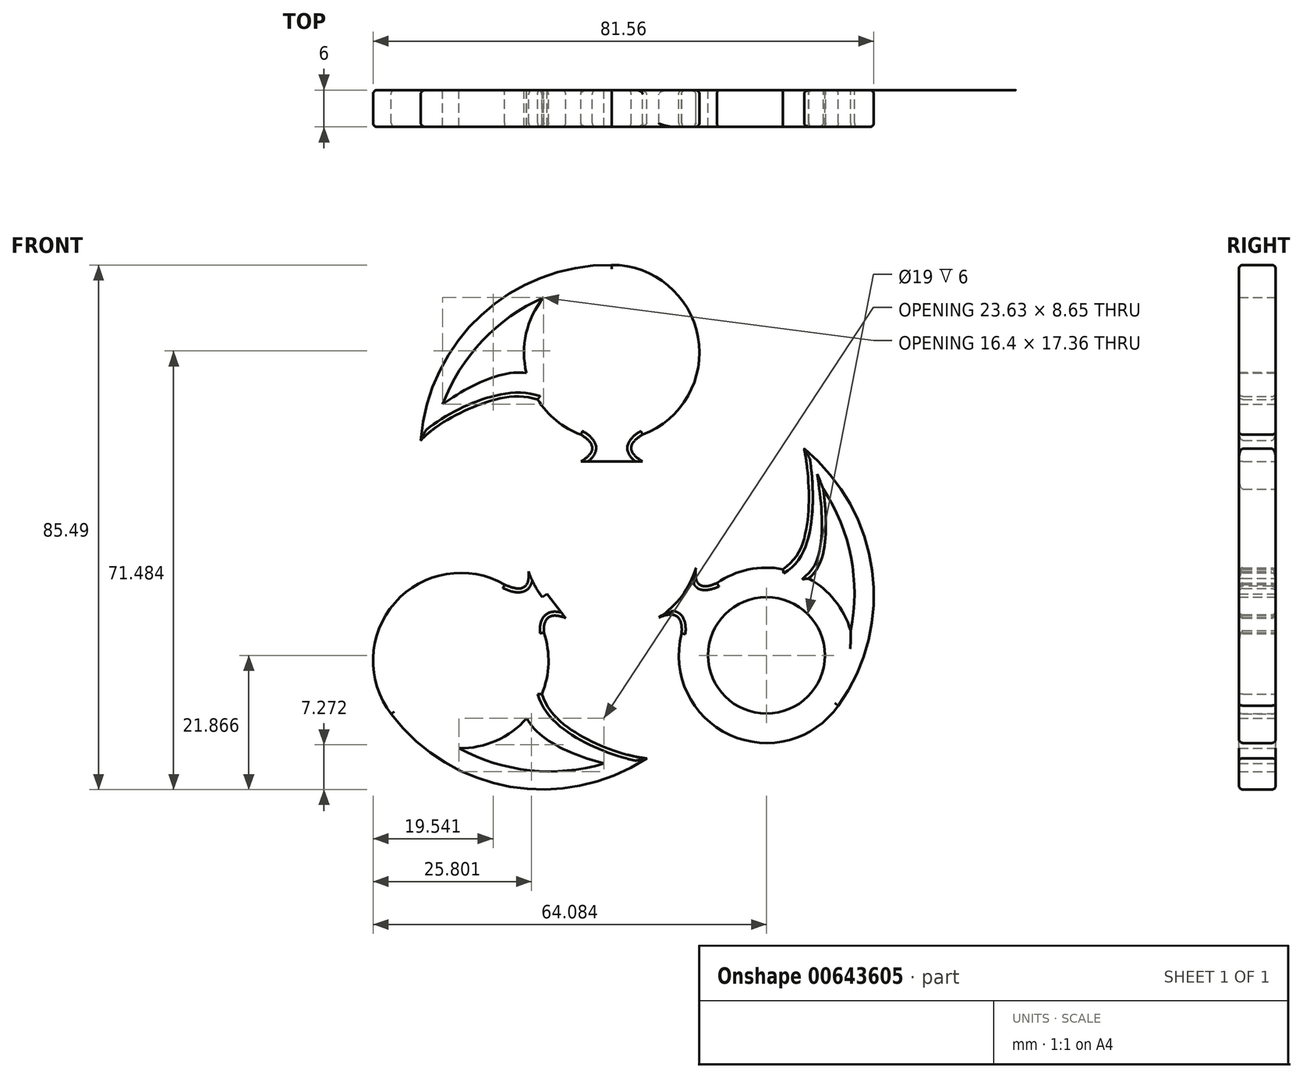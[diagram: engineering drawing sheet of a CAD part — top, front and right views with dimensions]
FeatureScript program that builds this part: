
annotation { "Feature Type Name" : "Feature", "Feature Type Description" : "" }
export const myFeature = defineFeature(function(context is Context, id is Id, definition is map)
    precondition{}
    {
        {
            var Q0;
            Q0=qCreatedBy(makeId("Front.planeOp"),FACE);
            var sketch = newSketch(context, id + "F0", { "sketchPlane" : qUnion([Q0])});
            skCircle(sketch, "E0", {"center": v(0, 0) * mm, "radius": 14.29 * mm});
            skLineSegment(sketch, "E1", {"start": v(0, 0) * mm, "end": v(0, 14.29) * mm});
            skLineSegment(sketch, "E2", {"start": v(0, 0) * mm, "end": v(-11.3, -8.76) * mm});
            skLineSegment(sketch, "E3", {"start": v(0, 0) * mm, "end": v(11.43, -8.57) * mm});
            skCircle(sketch, "E4", {"center": v(0, 31.12) * mm, "radius": 14.29 * mm});
            skLineSegment(sketch, "E5", {"start": v(0, 14.29) * mm, "end": v(0, 16.83) * mm});
            skArc(sketch, "E6", {"start": v(0, 45.4) * mm, "mid": v(-21.2, 37.27) * mm, "end": v(-31.1, 16.83) * mm});
            skFitSpline(sketch, "E7", {"points": [v(-31.1, 16.83) * mm, v(-17.35, 23.79) * mm, v(0, 16.83) * mm], "startDerivative": vector(18.3, 19.68) * mm, "endDerivative": vector(52.34, -33.11) * mm});
            skLineSegment(sketch, "E8", {"start": v(0, 15.56) * mm, "end": v(-3.18, 15.56) * mm});
            skPoint(sketch, "E8.endSnap0", {"position": v(0, 15.56) * mm});
            skLineSegment(sketch, "E9", {"start": v(0, 15.56) * mm, "end": v(3.18, 15.56) * mm});
            skLineSegment(sketch, "E10", {"start": v(0, 17.74) * mm, "end": v(5.03, 17.74) * mm});
            skLineSegment(sketch, "E11", {"start": v(0, 17.74) * mm, "end": v(-5.03, 17.74) * mm});
            skLineSegment(sketch, "E12", {"start": v(0, 14.29) * mm, "end": v(0, 13.37) * mm});
            skLineSegment(sketch, "E13", {"start": v(0, 13.37) * mm, "end": v(-5.03, 13.37) * mm});
            skLineSegment(sketch, "E14", {"start": v(0, 13.37) * mm, "end": v(5.03, 13.37) * mm});
            skFitSpline(sketch, "E15", {"points": [v(-5.03, 17.74) * mm, v(-3.18, 15.56) * mm, v(-5.03, 13.37) * mm], "startDerivative": vector(7.47, -4.37) * mm, "endDerivative": vector(-7.47, -4.37) * mm});
            skFitSpline(sketch, "E16", {"points": [v(5.03, 13.37) * mm, v(3.18, 15.56) * mm, v(5.03, 17.74) * mm], "startDerivative": vector(-7.47, 4.37) * mm, "endDerivative": vector(7.47, 4.37) * mm});
            skArc(sketch, "E17", {"start": v(4.36, 42.56) * mm, "mid": v(-16.61, 36.94) * mm, "end": v(-28.69, 18.9) * mm});
            skFitSpline(sketch, "E18", {"points": [v(-30.7, 19.98) * mm, v(-16.8, 27.72) * mm, v(0.44, 19.97) * mm], "startDerivative": vector(18.3, 19.68) * mm, "endDerivative": vector(52.34, -33.11) * mm});
            skLineSegment(sketch, "E19", {"start": v(-3.18, 15.56) * mm, "end": v(0, 14.29) * mm});
            skLineSegment(sketch, "E20", {"start": v(0, 14.29) * mm, "end": v(3.18, 15.56) * mm});
            skCircle(sketch, "E21", {"center": v(25.21, -18.22) * mm, "radius": 14.29 * mm});
            skLineSegment(sketch, "E22", {"start": v(11.43, -8.57) * mm, "end": v(13.51, -10.03) * mm});
            skArc(sketch, "E23", {"start": v(36.92, -26.42) * mm, "mid": v(42.42, -4.39) * mm, "end": v(31.34, 15.44) * mm});
            skFitSpline(sketch, "E24", {"points": [v(31.34, 15.44) * mm, v(30.71, -0.93) * mm, v(13.51, -10.03) * mm], "startDerivative": vector(5.62, -26.28) * mm, "endDerivative": vector(-57.15, -23.88) * mm});
            skLineSegment(sketch, "E25", {"start": v(12.47, -9.3) * mm, "end": v(14.3, -6.7) * mm});
            skPoint(sketch, "E25.endSnap0", {"position": v(12.47, -9.3) * mm});
            skLineSegment(sketch, "E26", {"start": v(12.47, -9.3) * mm, "end": v(10.65, -11.9) * mm});
            skLineSegment(sketch, "E27", {"start": v(14.26, -10.55) * mm, "end": v(11.38, -14.67) * mm});
            skLineSegment(sketch, "E28", {"start": v(14.26, -10.55) * mm, "end": v(17.14, -6.43) * mm});
            skArc(sketch, "E29", {"start": v(32.04, -28.23) * mm, "mid": v(39.54, -7.93) * mm, "end": v(31.84, 12.3) * mm});
            skFitSpline(sketch, "E30", {"points": [v(33.7, 13.3) * mm, v(33.83, -3.4) * mm, v(15.84, -12.2) * mm], "startDerivative": vector(5.62, -26.28) * mm, "endDerivative": vector(-57.15, -23.88) * mm});
            skLineSegment(sketch, "E31", {"start": v(14.3, -6.7) * mm, "end": v(11.8, -8.05) * mm});
            skLineSegment(sketch, "E32", {"start": v(11.43, -8.57) * mm, "end": v(10.65, -11.9) * mm});
            skLineSegment(sketch, "E33.0", {"start": v(14.3, -6.7) * mm, "end": v(12.47, -9.3) * mm, "construction": true});
            skCircle(sketch, "E34", {"center": v(-24.58, -19.07) * mm, "radius": 14.29 * mm});
            skLineSegment(sketch, "E35", {"start": v(-11.3, -8.76) * mm, "end": v(-13.26, -10.36) * mm});
            skArc(sketch, "E36", {"start": v(-35.91, -27.78) * mm, "mid": v(-16.54, -39.63) * mm, "end": v(5.7, -35.02) * mm});
            skFitSpline(sketch, "E37", {"points": [v(5.7, -35.02) * mm, v(-8.63, -28.76) * mm, v(-13.26, -10.36) * mm], "startDerivative": vector(-26.76, 2.52) * mm, "endDerivative": vector(-5.64, 61.68) * mm});
            skLineSegment(sketch, "E38", {"start": v(-12.27, -9.56) * mm, "end": v(-10.26, -12.02) * mm});
            skPoint(sketch, "E38.endSnap0", {"position": v(-12.27, -9.56) * mm});
            skLineSegment(sketch, "E39", {"start": v(-12.27, -9.56) * mm, "end": v(-14.28, -7.1) * mm});
            skLineSegment(sketch, "E40", {"start": v(-13.97, -10.94) * mm, "end": v(-17.43, -6.7) * mm});
            skLineSegment(sketch, "E41", {"start": v(-13.97, -10.94) * mm, "end": v(-11.04, -14.51) * mm});
            skArc(sketch, "E42", {"start": v(-36.27, -22.58) * mm, "mid": v(-19.07, -35.8) * mm, "end": v(2.57, -34.43) * mm});
            skFitSpline(sketch, "E43", {"points": [v(2.95, -36.62) * mm, v(-12.05, -30.77) * mm, v(-16.16, -11.65) * mm], "startDerivative": vector(-26.76, 2.52) * mm, "endDerivative": vector(-5.64, 61.68) * mm});
            skLineSegment(sketch, "E44", {"start": v(-10.26, -12.02) * mm, "end": v(-10.8, -9.23) * mm});
            skLineSegment(sketch, "E45", {"start": v(-11.3, -8.76) * mm, "end": v(-14.28, -7.1) * mm});
            skLineSegment(sketch, "E46.0", {"start": v(-10.26, -12.02) * mm, "end": v(-12.27, -9.56) * mm, "construction": true});
            skLineSegment(sketch, "E47", {"start": v(-11.3, -8.76) * mm, "end": v(-10.57, -8.2) * mm});
            skLineSegment(sketch, "E48", {"start": v(11.43, -8.57) * mm, "end": v(10.7, -8.02) * mm});
            skLineSegment(sketch, "E49", {"start": v(10.7, -8.02) * mm, "end": v(13.72, -4) * mm});
            skLineSegment(sketch, "E50", {"start": v(10.7, -8.02) * mm, "end": v(7.68, -12.05) * mm});
            skLineSegment(sketch, "E51", {"start": v(-10.57, -8.2) * mm, "end": v(-13.54, -4.56) * mm});
            skLineSegment(sketch, "E52", {"start": v(-10.57, -8.2) * mm, "end": v(-7.49, -12.17) * mm});
            skFitSpline(sketch, "E53", {"points": [v(-13.54, -4.56) * mm, v(-14.28, -7.1) * mm, v(-17.43, -6.7) * mm], "startDerivative": vector(0.73, -8.28) * mm, "endDerivative": vector(-8.38, 3.81) * mm});
            skFitSpline(sketch, "E54", {"points": [v(-11.04, -14.51) * mm, v(-10.26, -12.02) * mm, v(-7.49, -12.17) * mm], "startDerivative": vector(-0.57, 7.9) * mm, "endDerivative": vector(7.64, -3.14) * mm});
            skFitSpline(sketch, "E55", {"points": [v(7.68, -12.05) * mm, v(10.65, -11.9) * mm, v(11.38, -14.67) * mm], "startDerivative": vector(8.1, 3.32) * mm, "endDerivative": vector(-0.74, -8.6) * mm});
            skFitSpline(sketch, "E56", {"points": [v(13.72, -4) * mm, v(14.3, -6.7) * mm, v(17.14, -6.43) * mm], "startDerivative": vector(-1.06, -8.48) * mm, "endDerivative": vector(7.9, 3.59) * mm});
            skSolve(sketch);
        }
        {
            var Q0;
            {var subQ0=sQuery(id+"F0.wireOp",EDGE,"E6");var subQ1=sQuery(id+"F0.wireOp",EDGE,"E4");var subQ2=makeQuery(id+"F0.imprint","INTERSECT",VERTEX,{"derivedFrom":[subQ1,subQ0]});Q0=makeQuery(id+"F0.imprint","IMPRINT",FACE,{"disambiguationData":[TD([[makeQuery(id+"F0.imprint","IMPRINT",EDGE,{"disambiguationData":[TD([[subQ2,-1.0]])],"derivedFrom":subQ1}),-1.0]])]});}
            var Q1;
            {var subQ0=sQuery(id+"F0.wireOp",EDGE,"E18");var subQ1=sQuery(id+"F0.wireOp",EDGE,"E4");var subQ2=makeQuery(id+"F0.imprint","INTERSECT",VERTEX,{"derivedFrom":[subQ1,subQ0]});Q1=makeQuery(id+"F0.imprint","IMPRINT",FACE,{"disambiguationData":[TD([[makeQuery(id+"F0.imprint","IMPRINT",EDGE,{"disambiguationData":[TD([[subQ2,-1.0]])],"derivedFrom":subQ1}),-1.0]])]});}
            var Q2;
            {var subQ0=sQuery(id+"F0.wireOp",EDGE,"E7");var subQ1=sQuery(id+"F0.wireOp",EDGE,"E6");var subQ2=makeQuery(id+"F0.imprint","INTERSECT",VERTEX,{"derivedFrom":[subQ1,subQ0]});Q2=makeQuery(id+"F0.imprint","IMPRINT",FACE,{"disambiguationData":[TD([[makeQuery(id+"F0.imprint","IMPRINT",EDGE,{"disambiguationData":[TD([[subQ2,1.0]])],"derivedFrom":subQ1}),1.0]])]});}
            var Q3;
            {var subQ7=sQuery(id+"F0.wireOp",EDGE,"E10");Q3=makeQuery(id+"F0.imprint","IMPRINT",FACE,{"disambiguationData":[TD([[makeQuery(id+"F0.imprint","IMPRINT",EDGE,{"derivedFrom":subQ7}),1.0]])]});}
            var Q4;
            Q4=makeQuery(id+"F0.imprint","IMPRINT",FACE,{"disambiguationData":[TD([[makeQuery(id+"F0.imprint","IMPRINT",EDGE,{"derivedFrom":sQuery(id+"F0.wireOp",EDGE,"E1")}),1.0]])]});
            var Q5;
            Q5=makeQuery(id+"F0.imprint","IMPRINT",FACE,{"disambiguationData":[TD([[makeQuery(id+"F0.imprint","IMPRINT",EDGE,{"derivedFrom":sQuery(id+"F0.wireOp",EDGE,"E2")}),1.0]])]});
            var Q6;
            Q6=makeQuery(id+"F0.imprint","IMPRINT",FACE,{"disambiguationData":[TD([[makeQuery(id+"F0.imprint","IMPRINT",EDGE,{"derivedFrom":sQuery(id+"F0.wireOp",EDGE,"E1")}),-1.0]])]});
            var Q7;
            {var subQ7=sQuery(id+"F0.wireOp",EDGE,"E40");Q7=makeQuery(id+"F0.imprint","IMPRINT",FACE,{"disambiguationData":[TD([[makeQuery(id+"F0.imprint","IMPRINT",EDGE,{"derivedFrom":subQ7}),1.0]])]});}
            var Q8;
            {var subQ0=sQuery(id+"F0.wireOp",EDGE,"E36");var subQ1=sQuery(id+"F0.wireOp",EDGE,"E34");var subQ2=makeQuery(id+"F0.imprint","INTERSECT",VERTEX,{"derivedFrom":[subQ1,subQ0]});Q8=makeQuery(id+"F0.imprint","IMPRINT",FACE,{"disambiguationData":[TD([[makeQuery(id+"F0.imprint","IMPRINT",EDGE,{"disambiguationData":[TD([[subQ2,-1.0]])],"derivedFrom":subQ1}),-1.0]])]});}
            var Q9;
            {var subQ0=sQuery(id+"F0.wireOp",EDGE,"E43");var subQ1=sQuery(id+"F0.wireOp",EDGE,"E34");var subQ2=makeQuery(id+"F0.imprint","INTERSECT",VERTEX,{"derivedFrom":[subQ1,subQ0]});Q9=makeQuery(id+"F0.imprint","IMPRINT",FACE,{"disambiguationData":[TD([[makeQuery(id+"F0.imprint","IMPRINT",EDGE,{"disambiguationData":[TD([[subQ2,-1.0]])],"derivedFrom":subQ1}),-1.0]])]});}
            var Q10;
            {var subQ0=sQuery(id+"F0.wireOp",EDGE,"E37");var subQ1=sQuery(id+"F0.wireOp",EDGE,"E36");var subQ2=makeQuery(id+"F0.imprint","INTERSECT",VERTEX,{"derivedFrom":[subQ1,subQ0]});Q10=makeQuery(id+"F0.imprint","IMPRINT",FACE,{"disambiguationData":[TD([[makeQuery(id+"F0.imprint","IMPRINT",EDGE,{"disambiguationData":[TD([[subQ2,1.0]])],"derivedFrom":subQ1}),1.0]])]});}
            var Q11;
            {var subQ1=sQuery(id+"F0.wireOp",EDGE,"E34");var subQ3=sQuery(id+"F0.wireOp",EDGE,"E37");var subQ4=makeQuery(id+"F0.imprint","INTERSECT",VERTEX,{"derivedFrom":[subQ1,subQ3]});Q11=makeQuery(id+"F0.imprint","IMPRINT",FACE,{"disambiguationData":[TD([[makeQuery(id+"F0.imprint","IMPRINT",EDGE,{"disambiguationData":[TD([[subQ4,-1.0]])],"derivedFrom":subQ3}),-1.0]])]});}
            var Q12;
            {var subQ5=sQuery(id+"F0.wireOp",EDGE,"E27");Q12=makeQuery(id+"F0.imprint","IMPRINT",FACE,{"disambiguationData":[TD([[makeQuery(id+"F0.imprint","IMPRINT",EDGE,{"derivedFrom":subQ5}),1.0]])]});}
            var Q13;
            {var subQ0=sQuery(id+"F0.wireOp",EDGE,"E23");var subQ1=sQuery(id+"F0.wireOp",EDGE,"E21");var subQ2=makeQuery(id+"F0.imprint","INTERSECT",VERTEX,{"derivedFrom":[subQ1,subQ0]});Q13=makeQuery(id+"F0.imprint","IMPRINT",FACE,{"disambiguationData":[TD([[makeQuery(id+"F0.imprint","IMPRINT",EDGE,{"disambiguationData":[TD([[subQ2,-1.0]])],"derivedFrom":subQ1}),-1.0]])]});}
            var Q14;
            {var subQ0=sQuery(id+"F0.wireOp",EDGE,"E30");var subQ1=sQuery(id+"F0.wireOp",EDGE,"E21");var subQ2=makeQuery(id+"F0.imprint","INTERSECT",VERTEX,{"derivedFrom":[subQ1,subQ0]});Q14=makeQuery(id+"F0.imprint","IMPRINT",FACE,{"disambiguationData":[TD([[makeQuery(id+"F0.imprint","IMPRINT",EDGE,{"disambiguationData":[TD([[subQ2,-1.0]])],"derivedFrom":subQ1}),-1.0]])]});}
            var Q15;
            {var subQ0=sQuery(id+"F0.wireOp",EDGE,"E24");var subQ1=sQuery(id+"F0.wireOp",EDGE,"E23");var subQ2=makeQuery(id+"F0.imprint","INTERSECT",VERTEX,{"derivedFrom":[subQ1,subQ0]});Q15=makeQuery(id+"F0.imprint","IMPRINT",FACE,{"disambiguationData":[TD([[makeQuery(id+"F0.imprint","IMPRINT",EDGE,{"disambiguationData":[TD([[subQ2,1.0]])],"derivedFrom":subQ1}),1.0]])]});}
            var Q16;
            {var subQ0=sQuery(id+"F0.wireOp",EDGE,"E28");var subQ1=sQuery(id+"F0.wireOp",EDGE,"E21");var subQ2=makeQuery(id+"F0.imprint","INTERSECT",VERTEX,{"derivedFrom":[subQ1,subQ0]});Q16=makeQuery(id+"F0.imprint","IMPRINT",FACE,{"disambiguationData":[TD([[makeQuery(id+"F0.imprint","IMPRINT",EDGE,{"disambiguationData":[TD([[subQ2,1.0]])],"derivedFrom":subQ1}),1.0]])]});}
            var Q17;
            {var subQ3=sQuery(id+"F0.wireOp",EDGE,"E40");Q17=makeQuery(id+"F0.imprint","IMPRINT",FACE,{"disambiguationData":[TD([[makeQuery(id+"F0.imprint","IMPRINT",EDGE,{"derivedFrom":subQ3}),-1.0]])]});}
            var Q18;
            {var subQ0=sQuery(id+"F0.wireOp",EDGE,"E37");var subQ3=sQuery(id+"F0.wireOp",EDGE,"E41");var subQ5=makeQuery(id+"F0.imprint","INTERSECT",VERTEX,{"derivedFrom":[subQ0,subQ3]});Q18=makeQuery(id+"F0.imprint","IMPRINT",FACE,{"disambiguationData":[TD([[makeQuery(id+"F0.imprint","IMPRINT",EDGE,{"disambiguationData":[TD([[subQ5,-1.0]])],"derivedFrom":subQ0}),-1.0]])]});}
            var Q19;
            {var subQ0=sQuery(id+"F0.wireOp",EDGE,"E47");Q19=makeQuery(id+"F0.imprint","IMPRINT",FACE,{"disambiguationData":[TD([[makeQuery(id+"F0.imprint","IMPRINT",EDGE,{"derivedFrom":subQ0}),-1.0]])]});}
            var Q20;
            {var subQ0=sQuery(id+"F0.wireOp",EDGE,"E47");Q20=makeQuery(id+"F0.imprint","IMPRINT",FACE,{"disambiguationData":[TD([[makeQuery(id+"F0.imprint","IMPRINT",EDGE,{"derivedFrom":subQ0}),1.0]])]});}
            var Q21;
            {var subQ0=sQuery(id+"F0.wireOp",EDGE,"E45");Q21=makeQuery(id+"F0.imprint","IMPRINT",FACE,{"disambiguationData":[TD([[makeQuery(id+"F0.imprint","IMPRINT",EDGE,{"derivedFrom":subQ0}),-1.0]])]});}
            var Q22;
            {var subQ1=sQuery(id+"F0.wireOp",EDGE,"E0");var subQ3=sQuery(id+"F0.wireOp",EDGE,"E44");var subQ4=makeQuery(id+"F0.imprint","INTERSECT",VERTEX,{"derivedFrom":[subQ1,subQ3]});Q22=makeQuery(id+"F0.imprint","IMPRINT",FACE,{"disambiguationData":[TD([[makeQuery(id+"F0.imprint","IMPRINT",EDGE,{"disambiguationData":[TD([[subQ4,-1.0]])],"derivedFrom":subQ1}),-1.0]])]});}
            var Q23;
            {var subQ5=sQuery(id+"F0.wireOp",EDGE,"E38");Q23=makeQuery(id+"F0.imprint","IMPRINT",FACE,{"disambiguationData":[TD([[makeQuery(id+"F0.imprint","IMPRINT",EDGE,{"derivedFrom":subQ5}),-1.0]])]});}
            var Q24;
            {var subQ5=sQuery(id+"F0.wireOp",EDGE,"E39");Q24=makeQuery(id+"F0.imprint","IMPRINT",FACE,{"disambiguationData":[TD([[makeQuery(id+"F0.imprint","IMPRINT",EDGE,{"derivedFrom":subQ5}),1.0]])]});}
            var Q25;
            {var subQ2=sQuery(id+"F0.wireOp",EDGE,"E39");Q25=makeQuery(id+"F0.imprint","IMPRINT",FACE,{"disambiguationData":[TD([[makeQuery(id+"F0.imprint","IMPRINT",EDGE,{"derivedFrom":subQ2}),-1.0]])]});}
            var Q26;
            {var subQ5=sQuery(id+"F0.wireOp",EDGE,"E38");Q26=makeQuery(id+"F0.imprint","IMPRINT",FACE,{"disambiguationData":[TD([[makeQuery(id+"F0.imprint","IMPRINT",EDGE,{"derivedFrom":subQ5}),1.0]])]});}
            var Q27;
            {var subQ3=sQuery(id+"F0.wireOp",EDGE,"E27");Q27=makeQuery(id+"F0.imprint","IMPRINT",FACE,{"disambiguationData":[TD([[makeQuery(id+"F0.imprint","IMPRINT",EDGE,{"derivedFrom":subQ3}),-1.0]])]});}
            var Q28;
            {var subQ0=sQuery(id+"F0.wireOp",EDGE,"E24");var subQ3=sQuery(id+"F0.wireOp",EDGE,"E28");var subQ5=makeQuery(id+"F0.imprint","INTERSECT",VERTEX,{"derivedFrom":[subQ0,subQ3]});Q28=makeQuery(id+"F0.imprint","IMPRINT",FACE,{"disambiguationData":[TD([[makeQuery(id+"F0.imprint","IMPRINT",EDGE,{"disambiguationData":[TD([[subQ5,-1.0]])],"derivedFrom":subQ0}),-1.0]])]});}
            var Q29;
            {var subQ5=sQuery(id+"F0.wireOp",EDGE,"E25");Q29=makeQuery(id+"F0.imprint","IMPRINT",FACE,{"disambiguationData":[TD([[makeQuery(id+"F0.imprint","IMPRINT",EDGE,{"derivedFrom":subQ5}),-1.0]])]});}
            var Q30;
            {var subQ2=sQuery(id+"F0.wireOp",EDGE,"E25");Q30=makeQuery(id+"F0.imprint","IMPRINT",FACE,{"disambiguationData":[TD([[makeQuery(id+"F0.imprint","IMPRINT",EDGE,{"derivedFrom":subQ2}),1.0]])]});}
            var Q31;
            {var subQ0=sQuery(id+"F0.wireOp",EDGE,"E31");Q31=makeQuery(id+"F0.imprint","IMPRINT",FACE,{"disambiguationData":[TD([[makeQuery(id+"F0.imprint","IMPRINT",EDGE,{"derivedFrom":subQ0}),-1.0]])]});}
            var Q32;
            {var subQ0=sQuery(id+"F0.wireOp",EDGE,"E48");Q32=makeQuery(id+"F0.imprint","IMPRINT",FACE,{"disambiguationData":[TD([[makeQuery(id+"F0.imprint","IMPRINT",EDGE,{"derivedFrom":subQ0}),-1.0]])]});}
            var Q33;
            {var subQ0=sQuery(id+"F0.wireOp",EDGE,"E48");Q33=makeQuery(id+"F0.imprint","IMPRINT",FACE,{"disambiguationData":[TD([[makeQuery(id+"F0.imprint","IMPRINT",EDGE,{"derivedFrom":subQ0}),1.0]])]});}
            var Q34;
            {var subQ0=sQuery(id+"F0.wireOp",EDGE,"E32");Q34=makeQuery(id+"F0.imprint","IMPRINT",FACE,{"disambiguationData":[TD([[makeQuery(id+"F0.imprint","IMPRINT",EDGE,{"derivedFrom":subQ0}),-1.0]])]});}
            var Q35;
            {var subQ2=sQuery(id+"F0.wireOp",EDGE,"E26");Q35=makeQuery(id+"F0.imprint","IMPRINT",FACE,{"disambiguationData":[TD([[makeQuery(id+"F0.imprint","IMPRINT",EDGE,{"derivedFrom":subQ2}),-1.0]])]});}
            var Q36;
            {var subQ5=sQuery(id+"F0.wireOp",EDGE,"E26");Q36=makeQuery(id+"F0.imprint","IMPRINT",FACE,{"disambiguationData":[TD([[makeQuery(id+"F0.imprint","IMPRINT",EDGE,{"derivedFrom":subQ5}),1.0]])]});}
            var Q37;
            {var subQ1=sQuery(id+"F0.wireOp",EDGE,"E4");var subQ3=sQuery(id+"F0.wireOp",EDGE,"E7");var subQ4=makeQuery(id+"F0.imprint","INTERSECT",VERTEX,{"derivedFrom":[subQ1,subQ3]});Q37=makeQuery(id+"F0.imprint","IMPRINT",FACE,{"disambiguationData":[TD([[makeQuery(id+"F0.imprint","IMPRINT",EDGE,{"disambiguationData":[TD([[subQ4,-1.0]])],"derivedFrom":subQ3}),-1.0]])]});}
            var Q38;
            {var subQ0=sQuery(id+"F0.wireOp",EDGE,"E7");var subQ3=sQuery(id+"F0.wireOp",EDGE,"E11");var subQ5=makeQuery(id+"F0.imprint","INTERSECT",VERTEX,{"derivedFrom":[subQ0,subQ3]});Q38=makeQuery(id+"F0.imprint","IMPRINT",FACE,{"disambiguationData":[TD([[makeQuery(id+"F0.imprint","IMPRINT",EDGE,{"disambiguationData":[TD([[subQ5,-1.0]])],"derivedFrom":subQ0}),-1.0]])]});}
            var Q39;
            {var subQ5=sQuery(id+"F0.wireOp",EDGE,"E8");Q39=makeQuery(id+"F0.imprint","IMPRINT",FACE,{"disambiguationData":[TD([[makeQuery(id+"F0.imprint","IMPRINT",EDGE,{"derivedFrom":subQ5}),-1.0]])]});}
            var Q40;
            {var subQ0=sQuery(id+"F0.wireOp",EDGE,"E20");Q40=makeQuery(id+"F0.imprint","IMPRINT",FACE,{"disambiguationData":[TD([[makeQuery(id+"F0.imprint","IMPRINT",EDGE,{"derivedFrom":subQ0}),-1.0]])]});}
            var Q41;
            {var subQ0=sQuery(id+"F0.wireOp",EDGE,"E12");Q41=makeQuery(id+"F0.imprint","IMPRINT",FACE,{"disambiguationData":[TD([[makeQuery(id+"F0.imprint","IMPRINT",EDGE,{"derivedFrom":subQ0}),1.0]])]});}
            var Q42;
            {var subQ0=sQuery(id+"F0.wireOp",EDGE,"E12");Q42=makeQuery(id+"F0.imprint","IMPRINT",FACE,{"disambiguationData":[TD([[makeQuery(id+"F0.imprint","IMPRINT",EDGE,{"derivedFrom":subQ0}),-1.0]])]});}
            var Q43;
            {var subQ0=sQuery(id+"F0.wireOp",EDGE,"E19");Q43=makeQuery(id+"F0.imprint","IMPRINT",FACE,{"disambiguationData":[TD([[makeQuery(id+"F0.imprint","IMPRINT",EDGE,{"derivedFrom":subQ0}),-1.0]])]});}
            var Q44;
            {var subQ2=sQuery(id+"F0.wireOp",EDGE,"E8");Q44=makeQuery(id+"F0.imprint","IMPRINT",FACE,{"disambiguationData":[TD([[makeQuery(id+"F0.imprint","IMPRINT",EDGE,{"derivedFrom":subQ2}),1.0]])]});}
            var Q45;
            {var subQ2=sQuery(id+"F0.wireOp",EDGE,"E9");Q45=makeQuery(id+"F0.imprint","IMPRINT",FACE,{"disambiguationData":[TD([[makeQuery(id+"F0.imprint","IMPRINT",EDGE,{"derivedFrom":subQ2}),-1.0]])]});}
            var Q46;
            {var subQ5=sQuery(id+"F0.wireOp",EDGE,"E9");Q46=makeQuery(id+"F0.imprint","IMPRINT",FACE,{"disambiguationData":[TD([[makeQuery(id+"F0.imprint","IMPRINT",EDGE,{"derivedFrom":subQ5}),1.0]])]});}
            var Q47;
            {var subQ3=sQuery(id+"F0.wireOp",EDGE,"E10");Q47=makeQuery(id+"F0.imprint","IMPRINT",FACE,{"disambiguationData":[TD([[makeQuery(id+"F0.imprint","IMPRINT",EDGE,{"derivedFrom":subQ3}),-1.0]])]});}
            extrude(context, id + "F1", {"entities" : qUnion([Q0, Q1, Q2, Q3, Q4, Q5, Q6, Q7, Q8, Q9, Q10, Q11, Q12, Q13, Q14, Q15, Q16, Q17, Q18, Q19, Q20, Q21, Q22, Q23, Q24, Q25, Q26, Q27, Q28, Q29, Q30, Q31, Q32, Q33, Q34, Q35, Q36, Q37, Q38, Q39, Q40, Q41, Q42, Q43, Q44, Q45, Q46, Q47]), "depth" : 6 * mm, "offsetDistance" : 25.4 * mm});
        }
        {
            var Q0;
            {var subQ0=sQuery(id+"F0.wireOp",EDGE,"E4");Q0=makeQuery(id+"F1.opExtrude","CAP_EDGE",EDGE,{"disambiguationData":[OSD([subQ0]),TDD([makeQuery(id+"F0.imprint","IMPRINT",EDGE,{"disambiguationData":[TD([[makeQuery(id+"F0.imprint","INTERSECT",VERTEX,{"derivedFrom":[subQ0,sQuery(id+"F0.wireOp",EDGE,"E7")]}),-1.0]])],"derivedFrom":subQ0})])],"isStart":false});}
            var Q1;
            Q1=makeQuery(id+"F1.opExtrude","CAP_EDGE",EDGE,{"disambiguationData":[OSD([sQuery(id+"F0.wireOp",EDGE,"E15")])],"isStart":false});
            var Q2;
            {var subQ0=sQuery(id+"F0.wireOp",EDGE,"E0");Q2=makeQuery(id+"F1.opExtrude","CAP_EDGE",EDGE,{"disambiguationData":[OSD([subQ0]),TDD([makeQuery(id+"F0.imprint","IMPRINT",EDGE,{"disambiguationData":[TD([[makeQuery(id+"F0.imprint","INTERSECT",VERTEX,{"derivedFrom":[subQ0,sQuery(id+"F0.wireOp",EDGE,"E13"),sQuery(id+"F0.wireOp",EDGE,"E15")]}),-1.0]])],"derivedFrom":subQ0})])],"isStart":false});}
            var Q3;
            Q3=makeQuery(id+"F1.opExtrude","CAP_EDGE",EDGE,{"disambiguationData":[OSD([sQuery(id+"F0.wireOp",EDGE,"E53")])],"isStart":false});
            var Q4;
            {var subQ0=sQuery(id+"F0.wireOp",EDGE,"E34");Q4=makeQuery(id+"F1.opExtrude","CAP_EDGE",EDGE,{"disambiguationData":[OSD([subQ0]),TDD([makeQuery(id+"F0.imprint","IMPRINT",EDGE,{"disambiguationData":[TD([[makeQuery(id+"F0.imprint","INTERSECT",VERTEX,{"derivedFrom":[subQ0,sQuery(id+"F0.wireOp",EDGE,"E36")]}),1.0]])],"derivedFrom":subQ0})])],"isStart":false});}
            var Q5;
            Q5=makeQuery(id+"F1.opExtrude","CAP_EDGE",EDGE,{"disambiguationData":[OSD([sQuery(id+"F0.wireOp",EDGE,"E36")])],"isStart":false});
            var Q6;
            Q6=makeQuery(id+"F1.opExtrude","CAP_EDGE",EDGE,{"disambiguationData":[OSD([sQuery(id+"F0.wireOp",EDGE,"E37")])],"isStart":false});
            var Q7;
            Q7=makeQuery(id+"F1.opExtrude","CAP_FACE",FACE,{"disambiguationData":[OSD([sQuery(id+"F0.wireOp",EDGE,"E0"),sQuery(id+"F0.wireOp",EDGE,"E4"),sQuery(id+"F0.wireOp",EDGE,"E6"),sQuery(id+"F0.wireOp",EDGE,"E7"),sQuery(id+"F0.wireOp",EDGE,"E15"),sQuery(id+"F0.wireOp",EDGE,"E16"),sQuery(id+"F0.wireOp",EDGE,"E17"),sQuery(id+"F0.wireOp",EDGE,"E18"),sQuery(id+"F0.wireOp",EDGE,"E21"),sQuery(id+"F0.wireOp",EDGE,"E23"),sQuery(id+"F0.wireOp",EDGE,"E24"),sQuery(id+"F0.wireOp",EDGE,"E29"),sQuery(id+"F0.wireOp",EDGE,"E30"),sQuery(id+"F0.wireOp",EDGE,"E34"),sQuery(id+"F0.wireOp",EDGE,"E36"),sQuery(id+"F0.wireOp",EDGE,"E37"),sQuery(id+"F0.wireOp",EDGE,"E42"),sQuery(id+"F0.wireOp",EDGE,"E43"),sQuery(id+"F0.wireOp",EDGE,"E53"),sQuery(id+"F0.wireOp",EDGE,"E54"),sQuery(id+"F0.wireOp",EDGE,"E55"),sQuery(id+"F0.wireOp",EDGE,"E56")])],"isStart":false});
            var Q8;
            Q8=makeQuery(id+"F1.opExtrude","CAP_EDGE",EDGE,{"disambiguationData":[OSD([sQuery(id+"F0.wireOp",EDGE,"E7")])],"isStart":false});
            var Q9;
            Q9=makeQuery(id+"F1.opExtrude","CAP_EDGE",EDGE,{"disambiguationData":[OSD([sQuery(id+"F0.wireOp",EDGE,"E54")])],"isStart":false});
            var Q10;
            {var subQ0=sQuery(id+"F0.wireOp",EDGE,"E34");Q10=makeQuery(id+"F1.opExtrude","CAP_EDGE",EDGE,{"disambiguationData":[OSD([subQ0]),TDD([makeQuery(id+"F0.imprint","IMPRINT",EDGE,{"disambiguationData":[TD([[makeQuery(id+"F0.imprint","INTERSECT",VERTEX,{"derivedFrom":[subQ0,sQuery(id+"F0.wireOp",EDGE,"E37")]}),-1.0]])],"derivedFrom":subQ0})])],"isStart":false});}
            var Q11;
            {var subQ0=sQuery(id+"F0.wireOp",EDGE,"E0");Q11=makeQuery(id+"F1.opExtrude","CAP_EDGE",EDGE,{"disambiguationData":[OSD([subQ0]),TDD([makeQuery(id+"F0.imprint","IMPRINT",EDGE,{"disambiguationData":[TD([[makeQuery(id+"F0.imprint","INTERSECT",VERTEX,{"derivedFrom":[subQ0,sQuery(id+"F0.wireOp",EDGE,"E50"),sQuery(id+"F0.wireOp",EDGE,"E55")]}),1.0]])],"derivedFrom":subQ0})])],"isStart":false});}
            var Q12;
            Q12=makeQuery(id+"F1.opExtrude","CAP_EDGE",EDGE,{"disambiguationData":[OSD([sQuery(id+"F0.wireOp",EDGE,"E55")])],"isStart":false});
            var Q13;
            {var subQ0=sQuery(id+"F0.wireOp",EDGE,"E21");Q13=makeQuery(id+"F1.opExtrude","CAP_EDGE",EDGE,{"disambiguationData":[OSD([subQ0]),TDD([makeQuery(id+"F0.imprint","IMPRINT",EDGE,{"disambiguationData":[TD([[makeQuery(id+"F0.imprint","INTERSECT",VERTEX,{"derivedFrom":[subQ0,sQuery(id+"F0.wireOp",EDGE,"E23")]}),1.0]])],"derivedFrom":subQ0})])],"isStart":false});}
            var Q14;
            Q14=makeQuery(id+"F1.opExtrude","CAP_EDGE",EDGE,{"disambiguationData":[OSD([sQuery(id+"F0.wireOp",EDGE,"E23")])],"isStart":false});
            var Q15;
            Q15=makeQuery(id+"F1.opExtrude","CAP_EDGE",EDGE,{"disambiguationData":[OSD([sQuery(id+"F0.wireOp",EDGE,"E24")])],"isStart":false});
            var Q16;
            {var subQ0=sQuery(id+"F0.wireOp",EDGE,"E21");Q16=makeQuery(id+"F1.opExtrude","CAP_EDGE",EDGE,{"disambiguationData":[OSD([subQ0]),TDD([makeQuery(id+"F0.imprint","IMPRINT",EDGE,{"disambiguationData":[TD([[makeQuery(id+"F0.imprint","INTERSECT",VERTEX,{"derivedFrom":[subQ0,sQuery(id+"F0.wireOp",EDGE,"E24")]}),-1.0]])],"derivedFrom":subQ0})])],"isStart":false});}
            var Q17;
            Q17=makeQuery(id+"F1.opExtrude","CAP_EDGE",EDGE,{"disambiguationData":[OSD([sQuery(id+"F0.wireOp",EDGE,"E56")])],"isStart":false});
            var Q18;
            {var subQ0=sQuery(id+"F0.wireOp",EDGE,"E0");Q18=makeQuery(id+"F1.opExtrude","CAP_EDGE",EDGE,{"disambiguationData":[OSD([subQ0]),TDD([makeQuery(id+"F0.imprint","IMPRINT",EDGE,{"disambiguationData":[TD([[makeQuery(id+"F0.imprint","INTERSECT",VERTEX,{"derivedFrom":[subQ0,sQuery(id+"F0.wireOp",EDGE,"E14"),sQuery(id+"F0.wireOp",EDGE,"E16")]}),1.0]])],"derivedFrom":subQ0})])],"isStart":false});}
            var Q19;
            Q19=makeQuery(id+"F1.opExtrude","CAP_EDGE",EDGE,{"disambiguationData":[OSD([sQuery(id+"F0.wireOp",EDGE,"E16")])],"isStart":false});
            var Q20;
            {var subQ0=sQuery(id+"F0.wireOp",EDGE,"E4");Q20=makeQuery(id+"F1.opExtrude","CAP_EDGE",EDGE,{"disambiguationData":[OSD([subQ0]),TDD([makeQuery(id+"F0.imprint","IMPRINT",EDGE,{"disambiguationData":[TD([[makeQuery(id+"F0.imprint","INTERSECT",VERTEX,{"derivedFrom":[subQ0,sQuery(id+"F0.wireOp",EDGE,"E6")]}),1.0]])],"derivedFrom":subQ0})])],"isStart":false});}
            var Q21;
            Q21=makeQuery(id+"F1.opExtrude","CAP_EDGE",EDGE,{"disambiguationData":[OSD([sQuery(id+"F0.wireOp",EDGE,"E6")])],"isStart":false});
            var Q22;
            Q22=makeQuery(id+"F1.opExtrude","CAP_EDGE",EDGE,{"disambiguationData":[OSD([sQuery(id+"F0.wireOp",EDGE,"E16")])],"isStart":true});
            var Q23;
            {var subQ0=sQuery(id+"F0.wireOp",EDGE,"E4");Q23=makeQuery(id+"F1.opExtrude","CAP_EDGE",EDGE,{"disambiguationData":[OSD([subQ0]),TDD([makeQuery(id+"F0.imprint","IMPRINT",EDGE,{"disambiguationData":[TD([[makeQuery(id+"F0.imprint","INTERSECT",VERTEX,{"derivedFrom":[subQ0,sQuery(id+"F0.wireOp",EDGE,"E6")]}),1.0]])],"derivedFrom":subQ0})])],"isStart":true});}
            var Q24;
            {var subQ0=sQuery(id+"F0.wireOp",EDGE,"E0");Q24=makeQuery(id+"F1.opExtrude","CAP_EDGE",EDGE,{"disambiguationData":[OSD([subQ0]),TDD([makeQuery(id+"F0.imprint","IMPRINT",EDGE,{"disambiguationData":[TD([[makeQuery(id+"F0.imprint","INTERSECT",VERTEX,{"derivedFrom":[subQ0,sQuery(id+"F0.wireOp",EDGE,"E14"),sQuery(id+"F0.wireOp",EDGE,"E16")]}),1.0]])],"derivedFrom":subQ0})])],"isStart":true});}
            var Q25;
            Q25=makeQuery(id+"F1.opExtrude","CAP_EDGE",EDGE,{"disambiguationData":[OSD([sQuery(id+"F0.wireOp",EDGE,"E56")])],"isStart":true});
            var Q26;
            {var subQ0=sQuery(id+"F0.wireOp",EDGE,"E21");Q26=makeQuery(id+"F1.opExtrude","CAP_EDGE",EDGE,{"disambiguationData":[OSD([subQ0]),TDD([makeQuery(id+"F0.imprint","IMPRINT",EDGE,{"disambiguationData":[TD([[makeQuery(id+"F0.imprint","INTERSECT",VERTEX,{"derivedFrom":[subQ0,sQuery(id+"F0.wireOp",EDGE,"E24")]}),-1.0]])],"derivedFrom":subQ0})])],"isStart":true});}
            var Q27;
            Q27=makeQuery(id+"F1.opExtrude","CAP_EDGE",EDGE,{"disambiguationData":[OSD([sQuery(id+"F0.wireOp",EDGE,"E23")])],"isStart":true});
            var Q28;
            Q28=makeQuery(id+"F1.opExtrude","CAP_EDGE",EDGE,{"disambiguationData":[OSD([sQuery(id+"F0.wireOp",EDGE,"E55")])],"isStart":true});
            var Q29;
            {var subQ0=sQuery(id+"F0.wireOp",EDGE,"E0");Q29=makeQuery(id+"F1.opExtrude","CAP_EDGE",EDGE,{"disambiguationData":[OSD([subQ0]),TDD([makeQuery(id+"F0.imprint","IMPRINT",EDGE,{"disambiguationData":[TD([[makeQuery(id+"F0.imprint","INTERSECT",VERTEX,{"derivedFrom":[subQ0,sQuery(id+"F0.wireOp",EDGE,"E50"),sQuery(id+"F0.wireOp",EDGE,"E55")]}),1.0]])],"derivedFrom":subQ0})])],"isStart":true});}
            var Q30;
            Q30=makeQuery(id+"F1.opExtrude","CAP_EDGE",EDGE,{"disambiguationData":[OSD([sQuery(id+"F0.wireOp",EDGE,"E54")])],"isStart":true});
            var Q31;
            {var subQ0=sQuery(id+"F0.wireOp",EDGE,"E34");Q31=makeQuery(id+"F1.opExtrude","CAP_EDGE",EDGE,{"disambiguationData":[OSD([subQ0]),TDD([makeQuery(id+"F0.imprint","IMPRINT",EDGE,{"disambiguationData":[TD([[makeQuery(id+"F0.imprint","INTERSECT",VERTEX,{"derivedFrom":[subQ0,sQuery(id+"F0.wireOp",EDGE,"E37")]}),-1.0]])],"derivedFrom":subQ0})])],"isStart":true});}
            var Q32;
            Q32=makeQuery(id+"F1.opExtrude","CAP_EDGE",EDGE,{"disambiguationData":[OSD([sQuery(id+"F0.wireOp",EDGE,"E37")])],"isStart":true});
            var Q33;
            Q33=makeQuery(id+"F1.opExtrude","CAP_EDGE",EDGE,{"disambiguationData":[OSD([sQuery(id+"F0.wireOp",EDGE,"E36")])],"isStart":true});
            var Q34;
            Q34=makeQuery(id+"F1.opExtrude","CAP_EDGE",EDGE,{"disambiguationData":[OSD([sQuery(id+"F0.wireOp",EDGE,"E36")])],"isStart":true});
            var Q35;
            {var subQ0=sQuery(id+"F0.wireOp",EDGE,"E34");Q35=makeQuery(id+"F1.opExtrude","CAP_EDGE",EDGE,{"disambiguationData":[OSD([subQ0]),TDD([makeQuery(id+"F0.imprint","IMPRINT",EDGE,{"disambiguationData":[TD([[makeQuery(id+"F0.imprint","INTERSECT",VERTEX,{"derivedFrom":[subQ0,sQuery(id+"F0.wireOp",EDGE,"E36")]}),1.0]])],"derivedFrom":subQ0})])],"isStart":true});}
            var Q36;
            Q36=makeQuery(id+"F1.opExtrude","CAP_EDGE",EDGE,{"disambiguationData":[OSD([sQuery(id+"F0.wireOp",EDGE,"E53")])],"isStart":true});
            var Q37;
            {var subQ0=sQuery(id+"F0.wireOp",EDGE,"E0");Q37=makeQuery(id+"F1.opExtrude","CAP_EDGE",EDGE,{"disambiguationData":[OSD([subQ0]),TDD([makeQuery(id+"F0.imprint","IMPRINT",EDGE,{"disambiguationData":[TD([[makeQuery(id+"F0.imprint","INTERSECT",VERTEX,{"derivedFrom":[subQ0,sQuery(id+"F0.wireOp",EDGE,"E13"),sQuery(id+"F0.wireOp",EDGE,"E15")]}),-1.0]])],"derivedFrom":subQ0})])],"isStart":true});}
            var Q38;
            Q38=makeQuery(id+"F1.opExtrude","CAP_EDGE",EDGE,{"disambiguationData":[OSD([sQuery(id+"F0.wireOp",EDGE,"E15")])],"isStart":true});
            var Q39;
            {var subQ0=sQuery(id+"F0.wireOp",EDGE,"E4");Q39=makeQuery(id+"F1.opExtrude","CAP_EDGE",EDGE,{"disambiguationData":[OSD([subQ0]),TDD([makeQuery(id+"F0.imprint","IMPRINT",EDGE,{"disambiguationData":[TD([[makeQuery(id+"F0.imprint","INTERSECT",VERTEX,{"derivedFrom":[subQ0,sQuery(id+"F0.wireOp",EDGE,"E7")]}),-1.0]])],"derivedFrom":subQ0})])],"isStart":true});}
            var Q40;
            Q40=makeQuery(id+"F1.opExtrude","CAP_EDGE",EDGE,{"disambiguationData":[OSD([sQuery(id+"F0.wireOp",EDGE,"E7")])],"isStart":true});
            var Q41;
            Q41=makeQuery(id+"F1.opExtrude","CAP_EDGE",EDGE,{"disambiguationData":[OSD([sQuery(id+"F0.wireOp",EDGE,"E6")])],"isStart":true});
            var Q42;
            {var subQ0=sQuery(id+"F0.wireOp",EDGE,"E21");Q42=makeQuery(id+"F1.opExtrude","CAP_EDGE",EDGE,{"disambiguationData":[OSD([subQ0]),TDD([makeQuery(id+"F0.imprint","IMPRINT",EDGE,{"disambiguationData":[TD([[makeQuery(id+"F0.imprint","INTERSECT",VERTEX,{"derivedFrom":[subQ0,sQuery(id+"F0.wireOp",EDGE,"E23")]}),1.0]])],"derivedFrom":subQ0})])],"isStart":true});}
            var Q43;
            Q43=makeQuery(id+"F1.opExtrude","CAP_EDGE",EDGE,{"disambiguationData":[OSD([sQuery(id+"F0.wireOp",EDGE,"E24")])],"isStart":true});
            fillet(context, id + "F2", {"entities" : qUnion([Q0, Q1, Q2, Q3, Q4, Q5, Q6, Q7, Q8, Q9, Q10, Q11, Q12, Q13, Q14, Q15, Q16, Q17, Q18, Q19, Q20, Q21, Q22, Q23, Q24, Q25, Q26, Q27, Q28, Q29, Q30, Q31, Q32, Q33, Q34, Q35, Q36, Q37, Q38, Q39, Q40, Q41, Q42, Q43]), "radius" : 0.64 * mm, "tangentPropagation" : true, "allowEdgeOverflow" : false});
        }
        {
            var Q0;
            Q0=sQuery(id+"F0.wireOp",VERTEX,"E3.start");
            var Q1;
            Q1=sQuery(id+"F0.wireOp",VERTEX,"E4.center");
            var Q2;
            Q2=sQuery(id+"F0.wireOp",VERTEX,"E34.center");
            var Q3;
            Q3=sQuery(id+"F0.wireOp",VERTEX,"E21.center");
            var Q4;
            Q4=makeQuery(id+"F1.opExtrude","SWEPT_BODY",BODY,{"disambiguationData":[OSD([sQuery(id+"F0.wireOp",EDGE,"E0"),sQuery(id+"F0.wireOp",EDGE,"E4"),sQuery(id+"F0.wireOp",EDGE,"E6"),sQuery(id+"F0.wireOp",EDGE,"E7"),sQuery(id+"F0.wireOp",EDGE,"E15"),sQuery(id+"F0.wireOp",EDGE,"E16"),sQuery(id+"F0.wireOp",EDGE,"E17"),sQuery(id+"F0.wireOp",EDGE,"E18"),sQuery(id+"F0.wireOp",EDGE,"E21"),sQuery(id+"F0.wireOp",EDGE,"E23"),sQuery(id+"F0.wireOp",EDGE,"E24"),sQuery(id+"F0.wireOp",EDGE,"E29"),sQuery(id+"F0.wireOp",EDGE,"E30"),sQuery(id+"F0.wireOp",EDGE,"E34"),sQuery(id+"F0.wireOp",EDGE,"E36"),sQuery(id+"F0.wireOp",EDGE,"E37"),sQuery(id+"F0.wireOp",EDGE,"E42"),sQuery(id+"F0.wireOp",EDGE,"E43"),sQuery(id+"F0.wireOp",EDGE,"E53"),sQuery(id+"F0.wireOp",EDGE,"E54"),sQuery(id+"F0.wireOp",EDGE,"E55"),sQuery(id+"F0.wireOp",EDGE,"E56")])]});
            hole(context, id + "F3", {"style" : HoleStyle.SIMPLE, "endStyle" : HoleEndStyle.THROUGH, "oppositeDirection" : true, "holeDiameter" : 19 * mm, "isTappedThrough" : true, "tappedDepth" : 12.7 * mm, "tapClearance" : 3, "locations" : qUnion([Q0, Q1, Q2, Q3]), "scope" : qUnion([Q4]), "majorDiameter" : 6.35 * mm});
        }
    });
